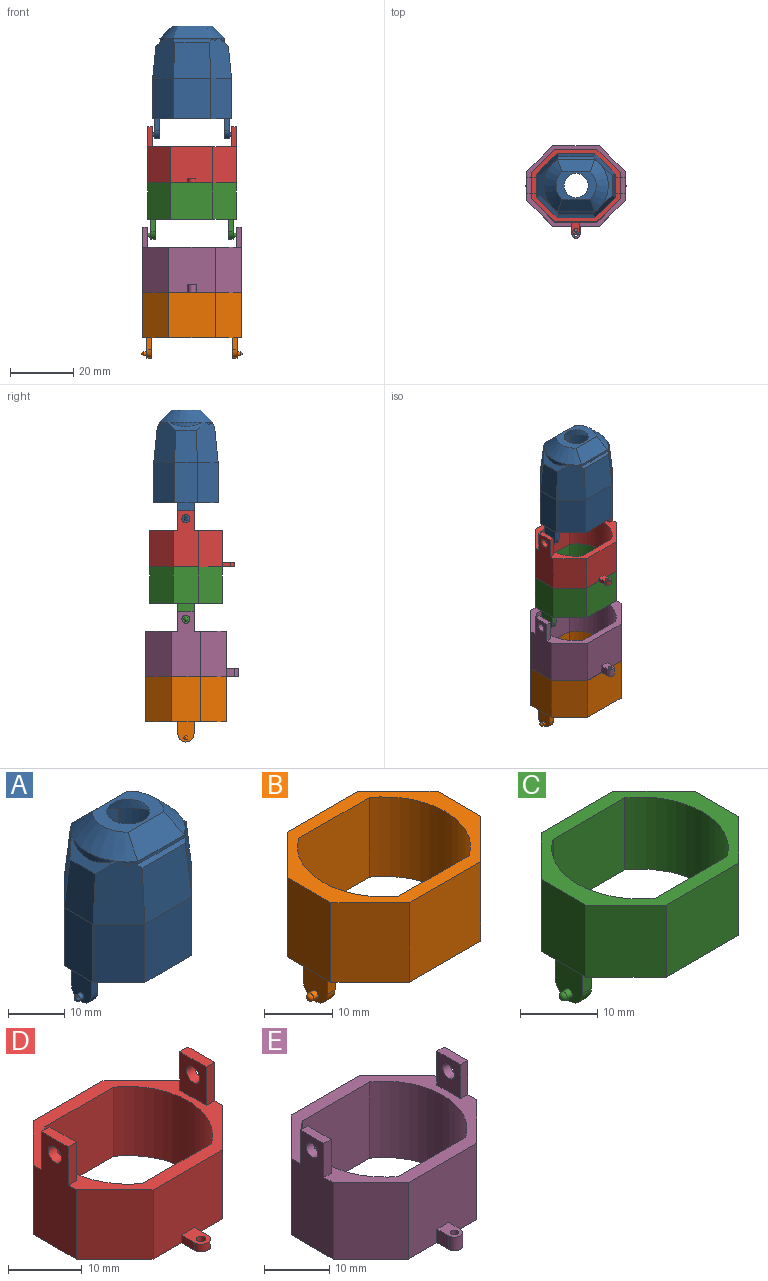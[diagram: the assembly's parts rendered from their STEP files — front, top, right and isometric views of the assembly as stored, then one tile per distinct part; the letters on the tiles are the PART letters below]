
ASSEMBLY  parts=5 mates=4
PART A: 57 faces, bbox 26.8x20.6x35.8 mm
  f0: plane 24.71x11.68mm, normal (0,1,0), area 281.2mm2, adj f2,f14,f15,f56
  f1: plane 24.71x11.68mm, normal (0,-1,0), area 281.2mm2, adj f2,f14,f15,f56
  f2: plane 24.88x20.32mm, normal (0,0,-1), area 109.5mm2, adj f0,f1,f7,f8,f9,f10,f11,f12
  f3: plane 0.96x0.68mm, normal (0,0,1), area 0.1mm2, adj f31,f33,f52
  f4: plane 0.96x0.68mm, normal (0,0,1), area 0.1mm2, adj f24,f32,f55
  f5: plane 0.96x0.68mm, normal (0,0,1), area 0.1mm2, adj f28,f33,f52
  f6: plane 0.96x0.68mm, normal (0,0,1), area 0.1mm2, adj f27,f32,f55
  f7: plane 12.7x6.53mm, normal (-0.71,0.71,0), area 117.3mm2, adj f2,f8,f16,f31
  f8: plane 12.7x7.26mm, normal (-1,0,0), area 92.2mm2, adj f2,f7,f9,f30
  f9: plane 12.7x6.53mm, normal (-0.71,-0.71,0), area 117.3mm2, adj f2,f8,f10,f28
  f10: plane 12.7x11.82mm, normal (0,-1,0), area 150.1mm2, adj f2,f9,f11,f26
  f11: plane 12.7x6.53mm, normal (0.71,-0.71,0), area 117.3mm2, adj f2,f10,f12,f24
  f12: plane 12.7x7.26mm, normal (1,0,0), area 92.2mm2, adj f2,f11,f13,f25
  f13: plane 12.7x6.53mm, normal (0.71,0.71,0), area 117.3mm2, adj f2,f12,f16,f27
  f14: cylinder r=10.16mm len=22.86mm, axis (0,0,-1), area 445.1mm2, adj f0,f1,f2,f56
  f15: cylinder r=10.16mm len=22.86mm, axis (0,0,-1), area 445.1mm2, adj f0,f1,f2,f56
  f16: plane 12.7x11.82mm, normal (0,1,0), area 150.1mm2, adj f2,f7,f13,f29
  f17: plane 6.35x5.08mm, normal (-1,0,0), area 29.5mm2, adj f2,f18,f20,f22
  f18: plane 3.81x1.57mm, normal (0,-1,0), area 6mm2, adj f2,f17,f19,f22
  f19: plane 6.35x5.08mm, normal (1,0,0), area 28.2mm2, adj f2,f18,f20,f21,f22
  f20: plane 3.81x1.57mm, normal (0,1,0), area 6mm2, adj f2,f17,f19,f22
  f21: cylinder r=0.64mm len=1.27mm, axis (-1,0,0), area 3.7mm2, adj f19,f23
  f22: cylinder r=2.54mm len=5.08mm, axis (1,0,0), area 12.5mm2, adj f17,f18,f19,f20
  f23: sphere r=0.64mm, area 2.5mm2, adj f21
  f24: plane 12.7x7.01mm, normal (0.7,-0.7,0.1), area 104.5mm2, adj f4,f11,f25,f26,f32,f35,f43
  f25: plane 10.17x7.26mm, normal (1,0,0.1), area 69.9mm2, adj f12,f24,f27,f32
  f26: plane 11.82x11.44mm, normal (0,-1,0.1), area 130.4mm2, adj f10,f24,f28,f35
  f27: plane 12.7x7.01mm, normal (0.7,0.7,0.1), area 104.5mm2, adj f6,f13,f25,f29,f32,f34,f48
  f28: plane 12.7x7.01mm, normal (-0.7,-0.7,0.1), area 104.5mm2, adj f5,f9,f26,f30,f33,f35,f46
  f29: plane 11.82x11.44mm, normal (0,1,0.1), area 130.4mm2, adj f16,f27,f31,f34
  f30: plane 10.17x7.26mm, normal (-1,0,0.1), area 69.9mm2, adj f8,f28,f31,f33
  f31: plane 12.7x7.01mm, normal (-0.7,0.7,0.1), area 104.5mm2, adj f3,f7,f29,f30,f33,f34,f50
  f32: plane 11.29x2.79mm, normal (0.67,0,0.74), area 18.4mm2, adj f4,f6,f24,f25,f27,f44
  f33: plane 11.29x2.79mm, normal (-0.67,0,0.74), area 18.4mm2, adj f3,f5,f28,f30,f31,f45
  f34: plane 12.94x1.19mm, normal (0,0.67,0.74), area 11mm2, adj f27,f29,f31,f48,f49,f50
  f35: plane 12.94x1.19mm, normal (0,-0.67,0.74), area 11mm2, adj f24,f26,f28,f43,f46,f47
  f36: sphere r=0.64mm, area 2.5mm2, adj f38
  f37: cylinder r=2.54mm len=5.08mm, axis (-1,0,0), area 12.5mm2, adj f39,f40,f41,f42
  f38: cylinder r=0.64mm len=1.27mm, axis (1,0,0), area 3.7mm2, adj f36,f40
  f39: plane 3.81x1.57mm, normal (0,1,0), area 6mm2, adj f2,f37,f40,f42
  f40: plane 6.35x5.08mm, normal (-1,0,0), area 28.2mm2, adj f2,f37,f38,f39,f41
  f41: plane 3.81x1.57mm, normal (0,-1,0), area 6mm2, adj f2,f37,f40,f42
  f42: plane 6.35x5.08mm, normal (1,0,0), area 29.5mm2, adj f2,f37,f39,f41
  f43: cylinder r=10.16mm len=2.11mm, axis (0,0,-1), area 1.3mm2, adj f24,f35,f47,f55
  f44: cylinder r=10.16mm len=10.72mm, axis (0,0,-1), area 10.3mm2, adj f32,f55
  f45: cylinder r=10.16mm len=10.72mm, axis (0,0,-1), area 10.3mm2, adj f33,f52
  f46: cylinder r=10.16mm len=2.11mm, axis (0,0,-1), area 1.3mm2, adj f28,f35,f47,f52
  f47: plane 11.68x0.63mm, normal (0,-1,0), area 7.3mm2, adj f35,f43,f46,f54
  f48: cylinder r=10.16mm len=2.11mm, axis (0,0,-1), area 1.3mm2, adj f27,f34,f49,f55
  f49: plane 11.68x0.63mm, normal (0,1,0), area 7.3mm2, adj f34,f48,f50,f53
  f50: cylinder r=10.16mm len=2.11mm, axis (0,0,-1), area 1.3mm2, adj f31,f34,f49,f52
  f51: plane 12.7x9.01mm, normal (0,0,1), area 58.3mm2, adj f52,f53,f54,f55,f56
  f52: cone r=10.16mm half-angle=45deg, axis (0,0,-1), area 78.3mm2, adj f3,f5,f45,f46,f50,f51,f53,f54
  f53: plane 11.93x4.06mm, normal (0,0.71,0.71), area 55.9mm2, adj f49,f51,f52,f55
  f54: plane 11.93x4.06mm, normal (0,-0.71,0.71), area 55.9mm2, adj f47,f51,f52,f55
  f55: cone r=10.16mm half-angle=45deg, axis (0,0,-1), area 78.3mm2, adj f4,f6,f43,f44,f48,f51,f53,f54
  f56: cone r=2.54mm half-angle=45deg, axis (0,0,-1), area 352.6mm2, adj f0,f1,f14,f15,f51
PART B: 28 faces, bbox 31.7x25.4x20.6 mm
  f0: plane 14.29x8.16mm, normal (-0.71,0.71,0), area 165mm2, adj f1,f11,f12,f27
  f1: plane 14.29x9.07mm, normal (-1,0,0), area 129.6mm2, adj f0,f2,f12,f27
  f2: plane 14.29x8.16mm, normal (-0.71,-0.71,0), area 165mm2, adj f1,f3,f12,f27
  f3: plane 14.78x14.29mm, normal (0,-1,0), area 211.1mm2, adj f2,f4,f12,f27
  f4: plane 14.29x8.16mm, normal (0.71,-0.71,0), area 165mm2, adj f3,f5,f12,f27
  f5: plane 14.29x9.07mm, normal (1,0,0), area 129.6mm2, adj f4,f6,f12,f27
  f6: plane 14.29x8.16mm, normal (0.71,0.71,0), area 165mm2, adj f5,f11,f12,f27
  f7: plane 14.6x14.29mm, normal (0,1,0), area 208.7mm2, adj f8,f10,f12,f27
  f8: cylinder r=12.7mm len=20.78mm, axis (0,0,-1), area 347.7mm2, adj f7,f9,f12,f27
  f9: plane 14.6x14.29mm, normal (0,-1,0), area 208.7mm2, adj f8,f10,f12,f27
  f10: cylinder r=12.7mm len=20.78mm, axis (0,0,-1), area 347.7mm2, adj f7,f9,f12,f27
  f11: plane 14.78x14.29mm, normal (0,1,0), area 211.1mm2, adj f0,f6,f12,f27
  f12: plane 31.11x25.4mm, normal (0,0,-1), area 180mm2, adj f0,f1,f2,f3,f4,f5,f6,f7
  f13: plane 6.35x5.08mm, normal (-1,0,0), area 29.5mm2, adj f12,f14,f16,f18
  f14: plane 3.81x1.57mm, normal (0,-1,0), area 6mm2, adj f12,f13,f15,f18
  f15: plane 6.35x5.08mm, normal (1,0,0), area 28.2mm2, adj f12,f14,f16,f17,f18
  f16: plane 3.81x1.57mm, normal (0,1,0), area 6mm2, adj f12,f13,f15,f18
  f17: cylinder r=0.64mm len=1.27mm, axis (-1,0,0), area 3.7mm2, adj f15,f19
  f18: cylinder r=2.54mm len=5.08mm, axis (1,0,0), area 12.5mm2, adj f13,f14,f15,f16
  f19: sphere r=0.64mm, area 2.5mm2, adj f17
  f20: sphere r=0.64mm, area 2.5mm2, adj f22
  f21: cylinder r=2.54mm len=5.08mm, axis (-1,0,0), area 12.5mm2, adj f23,f24,f25,f26
  f22: cylinder r=0.64mm len=1.27mm, axis (1,0,0), area 3.7mm2, adj f20,f24
  f23: plane 3.81x1.57mm, normal (0,1,0), area 6mm2, adj f12,f21,f24,f26
  f24: plane 6.35x5.08mm, normal (-1,0,0), area 28.2mm2, adj f12,f21,f22,f23,f25
  f25: plane 3.81x1.57mm, normal (0,-1,0), area 6mm2, adj f12,f21,f24,f26
  f26: plane 6.35x5.08mm, normal (1,0,0), area 29.5mm2, adj f12,f21,f23,f25
  f27: plane 31.11x25.4mm, normal (0,0,1), area 195.9mm2, adj f0,f1,f2,f3,f4,f5,f6,f7
PART C: 28 faces, bbox 29.1x22.9x17.8 mm
  f0: plane 11.43x7.35mm, normal (-0.71,0.71,0), area 118.8mm2, adj f1,f11,f12,f27
  f1: plane 11.43x8.17mm, normal (-1,0,0), area 93.3mm2, adj f0,f2,f12,f27
  f2: plane 11.43x7.35mm, normal (-0.71,-0.71,0), area 118.8mm2, adj f1,f3,f12,f27
  f3: plane 13.3x11.43mm, normal (0,-1,0), area 152mm2, adj f2,f4,f12,f27
  f4: plane 11.43x7.35mm, normal (0.71,-0.71,0), area 118.8mm2, adj f3,f5,f12,f27
  f5: plane 11.43x8.17mm, normal (1,0,0), area 93.3mm2, adj f4,f6,f12,f27
  f6: plane 11.43x7.35mm, normal (0.71,0.71,0), area 118.8mm2, adj f5,f11,f12,f27
  f7: plane 13.14x11.43mm, normal (0,1,0), area 150.2mm2, adj f8,f10,f12,f27
  f8: cylinder r=11.43mm len=18.7mm, axis (0,0,-1), area 250.4mm2, adj f7,f9,f12,f27
  f9: plane 13.14x11.43mm, normal (0,-1,0), area 150.2mm2, adj f8,f10,f12,f27
  f10: cylinder r=11.43mm len=18.7mm, axis (0,0,-1), area 250.4mm2, adj f7,f9,f12,f27
  f11: plane 13.3x11.43mm, normal (0,1,0), area 152mm2, adj f0,f6,f12,f27
  f12: plane 28x22.86mm, normal (0,0,-1), area 142.8mm2, adj f0,f1,f2,f3,f4,f5,f6,f7
  f13: plane 6.35x5.08mm, normal (-1,0,0), area 29.5mm2, adj f12,f14,f16,f18
  f14: plane 3.81x1.57mm, normal (0,-1,0), area 6mm2, adj f12,f13,f15,f18
  f15: plane 6.35x5.08mm, normal (1,0,0), area 28.2mm2, adj f12,f14,f16,f17,f18
  f16: plane 3.81x1.57mm, normal (0,1,0), area 6mm2, adj f12,f13,f15,f18
  f17: cylinder r=0.64mm len=1.27mm, axis (-1,0,0), area 3.7mm2, adj f15,f19
  f18: cylinder r=2.54mm len=5.08mm, axis (1,0,0), area 12.5mm2, adj f13,f14,f15,f16
  f19: sphere r=0.64mm, area 2.5mm2, adj f17
  f20: sphere r=0.64mm, area 2.5mm2, adj f22
  f21: cylinder r=2.54mm len=5.08mm, axis (-1,0,0), area 12.5mm2, adj f23,f24,f25,f26
  f22: cylinder r=0.64mm len=1.27mm, axis (1,0,0), area 3.7mm2, adj f20,f24
  f23: plane 3.81x1.57mm, normal (0,1,0), area 6mm2, adj f12,f21,f24,f26
  f24: plane 6.35x5.08mm, normal (-1,0,0), area 28.2mm2, adj f12,f21,f22,f23,f25
  f25: plane 3.81x1.57mm, normal (0,-1,0), area 6mm2, adj f12,f21,f24,f26
  f26: plane 6.35x5.08mm, normal (1,0,0), area 29.5mm2, adj f12,f21,f23,f25
  f27: plane 28x22.86mm, normal (0,0,1), area 158.7mm2, adj f0,f1,f2,f3,f4,f5,f6,f7
PART D: 29 faces, bbox 28x26.7x17.8 mm
  f0: plane 11.43x7.35mm, normal (-0.71,0.71,0), area 118.8mm2, adj f1,f9,f11,f23
  f1: plane 17.78x8.17mm, normal (-1,0,0), area 120.5mm2, adj f0,f2,f11,f19,f20,f21,f22,f23
  f2: plane 11.43x7.35mm, normal (-0.71,-0.71,0), area 118.8mm2, adj f1,f3,f11,f23
  f3: plane 13.3x11.43mm, normal (0,-1,0), area 148.8mm2, adj f2,f4,f11,f23,f24,f26,f28
  f4: plane 11.43x7.35mm, normal (0.71,-0.71,0), area 118.8mm2, adj f3,f5,f11,f23
  f5: plane 17.78x8.17mm, normal (1,0,0), area 120.5mm2, adj f4,f6,f11,f14,f15,f16,f17,f23
  f6: plane 11.43x7.35mm, normal (0.71,0.71,0), area 118.8mm2, adj f5,f9,f11,f23
  f7: cylinder r=11.43mm len=18.7mm, axis (0,0,-1), area 250.4mm2, adj f10,f11,f12,f23
  f8: cylinder r=11.43mm len=18.7mm, axis (0,0,-1), area 250.4mm2, adj f10,f11,f12,f23
  f9: plane 13.3x11.43mm, normal (0,1,0), area 152mm2, adj f0,f6,f11,f23
  f10: plane 13.14x11.43mm, normal (0,-1,0), area 150.2mm2, adj f7,f8,f11,f23
  f11: plane 28x22.86mm, normal (0,0,1), area 142.8mm2, adj f0,f1,f2,f3,f4,f5,f6,f7
  f12: plane 13.14x11.43mm, normal (0,1,0), area 150.2mm2, adj f7,f8,f11,f23
  f13: plane 6.35x5.08mm, normal (-1,0,0), area 27.2mm2, adj f11,f14,f15,f16,f17
  f14: plane 6.35x1.57mm, normal (0,-1,0), area 10mm2, adj f5,f11,f13,f16
  f15: plane 6.35x1.57mm, normal (0,1,0), area 10mm2, adj f5,f11,f13,f16
  f16: plane 5.08x1.57mm, normal (0,0,1), area 8mm2, adj f5,f13,f14,f15
  f17: cylinder r=1.27mm len=2.54mm, axis (1,0,0), area 12.5mm2, adj f5,f13
  f18: plane 6.35x5.08mm, normal (1,0,0), area 27.2mm2, adj f11,f19,f20,f21,f22
  f19: plane 6.35x1.57mm, normal (0,-1,0), area 10mm2, adj f1,f11,f18,f21
  f20: plane 6.35x1.57mm, normal (0,1,0), area 10mm2, adj f1,f11,f18,f21
  f21: plane 5.08x1.57mm, normal (0,0,1), area 8mm2, adj f1,f18,f19,f20
  f22: cylinder r=1.27mm len=2.54mm, axis (-1,0,0), area 12.5mm2, adj f1,f18
  f23: plane 28x26.67mm, normal (0,0,-1), area 166.4mm2, adj f0,f1,f2,f3,f4,f5,f6,f7
  f24: plane 2.54x1.27mm, normal (1,0,0), area 3.2mm2, adj f3,f23,f25,f28
  f25: cylinder r=1.27mm len=2.54mm, axis (0,0,-1), area 5.1mm2, adj f23,f24,f26,f28
  f26: plane 2.54x1.27mm, normal (-1,0,0), area 3.2mm2, adj f3,f23,f25,f28
  f27: cylinder r=0.64mm len=1.27mm, axis (0,0,-1), area 5.1mm2, adj f23,f28
  f28: plane 3.81x2.54mm, normal (0,0,1), area 7.7mm2, adj f3,f24,f25,f26,f27
PART E: 29 faces, bbox 31.1x29.2x20.6 mm
  f0: plane 14.29x8.16mm, normal (-0.71,0.71,0), area 165mm2, adj f1,f11,f12,f23
  f1: plane 20.64x9.07mm, normal (-1,0,0), area 156.8mm2, adj f0,f2,f12,f19,f20,f21,f22,f23
  f2: plane 14.29x8.16mm, normal (-0.71,-0.71,0), area 165mm2, adj f1,f3,f12,f23
  f3: plane 14.78x14.29mm, normal (0,-1,0), area 204.7mm2, adj f2,f4,f12,f23,f24,f26,f28
  f4: plane 14.29x8.16mm, normal (0.71,-0.71,0), area 165mm2, adj f3,f5,f12,f23
  f5: plane 20.64x9.07mm, normal (1,0,0), area 156.8mm2, adj f4,f6,f12,f14,f15,f16,f17,f23
  f6: plane 14.29x8.16mm, normal (0.71,0.71,0), area 165mm2, adj f5,f11,f12,f23
  f7: plane 14.6x14.29mm, normal (0,1,0), area 208.7mm2, adj f8,f10,f12,f23
  f8: cylinder r=12.7mm len=20.78mm, axis (0,0,-1), area 347.7mm2, adj f7,f9,f12,f23
  f9: plane 14.6x14.29mm, normal (0,-1,0), area 208.7mm2, adj f8,f10,f12,f23
  f10: cylinder r=12.7mm len=20.78mm, axis (0,0,-1), area 347.7mm2, adj f7,f9,f12,f23
  f11: plane 14.78x14.29mm, normal (0,1,0), area 211.1mm2, adj f0,f6,f12,f23
  f12: plane 31.11x25.4mm, normal (0,0,1), area 180mm2, adj f0,f1,f2,f3,f4,f5,f6,f7
  f13: plane 6.35x5.08mm, normal (-1,0,0), area 27.2mm2, adj f12,f14,f15,f16,f17
  f14: plane 6.35x1.57mm, normal (0,-1,0), area 10mm2, adj f5,f12,f13,f16
  f15: plane 6.35x1.57mm, normal (0,1,0), area 10mm2, adj f5,f12,f13,f16
  f16: plane 5.08x1.57mm, normal (0,0,1), area 8mm2, adj f5,f13,f14,f15
  f17: cylinder r=1.27mm len=2.54mm, axis (1,0,0), area 12.5mm2, adj f5,f13
  f18: plane 6.35x5.08mm, normal (1,0,0), area 27.2mm2, adj f12,f19,f20,f21,f22
  f19: plane 6.35x1.57mm, normal (0,-1,0), area 10mm2, adj f1,f12,f18,f21
  f20: plane 6.35x1.57mm, normal (0,1,0), area 10mm2, adj f1,f12,f18,f21
  f21: plane 5.08x1.57mm, normal (0,0,1), area 8mm2, adj f1,f18,f19,f20
  f22: cylinder r=1.27mm len=2.54mm, axis (-1,0,0), area 12.5mm2, adj f1,f18
  f23: plane 31.11x29.21mm, normal (0,0,-1), area 203.7mm2, adj f0,f1,f2,f3,f4,f5,f6,f7
  f24: plane 2.54x2.54mm, normal (1,0,0), area 6.5mm2, adj f3,f23,f25,f28
  f25: cylinder r=1.27mm len=2.54mm, axis (0,0,-1), area 10.1mm2, adj f23,f24,f26,f28
  f26: plane 2.54x2.54mm, normal (-1,0,0), area 6.5mm2, adj f3,f23,f25,f28
  f27: cylinder r=0.64mm len=2.54mm, axis (0,0,-1), area 10.1mm2, adj f23,f28
  f28: plane 3.81x2.54mm, normal (0,0,1), area 7.7mm2, adj f3,f24,f25,f26,f27
PLACE A t=(12.9,-14.49,8.88)mm
PLACE B t=(12.87,-14.49,-60.34)mm
PLACE C t=(12.84,-14.49,-22.87)mm
PLACE D t=(12.84,-14.49,-22.87)mm
PLACE E t=(12.87,-14.49,-60.34)mm
MATE revolute C.f17 <-> E.f17  axis (1,0,0) through (25.84,-14.49,-27.95)mm
MATE revolute A.f21 <-> D.f17  axis (1,0,0) through (24.63,-14.49,3.8)mm
MATE fastened B.f4 <-> E.f4  axis (0.71,-0.71,0) through (24.34,-23.1,-46.05)mm
MATE fastened C.f4 <-> D.f4  axis (0.71,-0.71,0) through (23.16,-22.24,-11.44)mm
